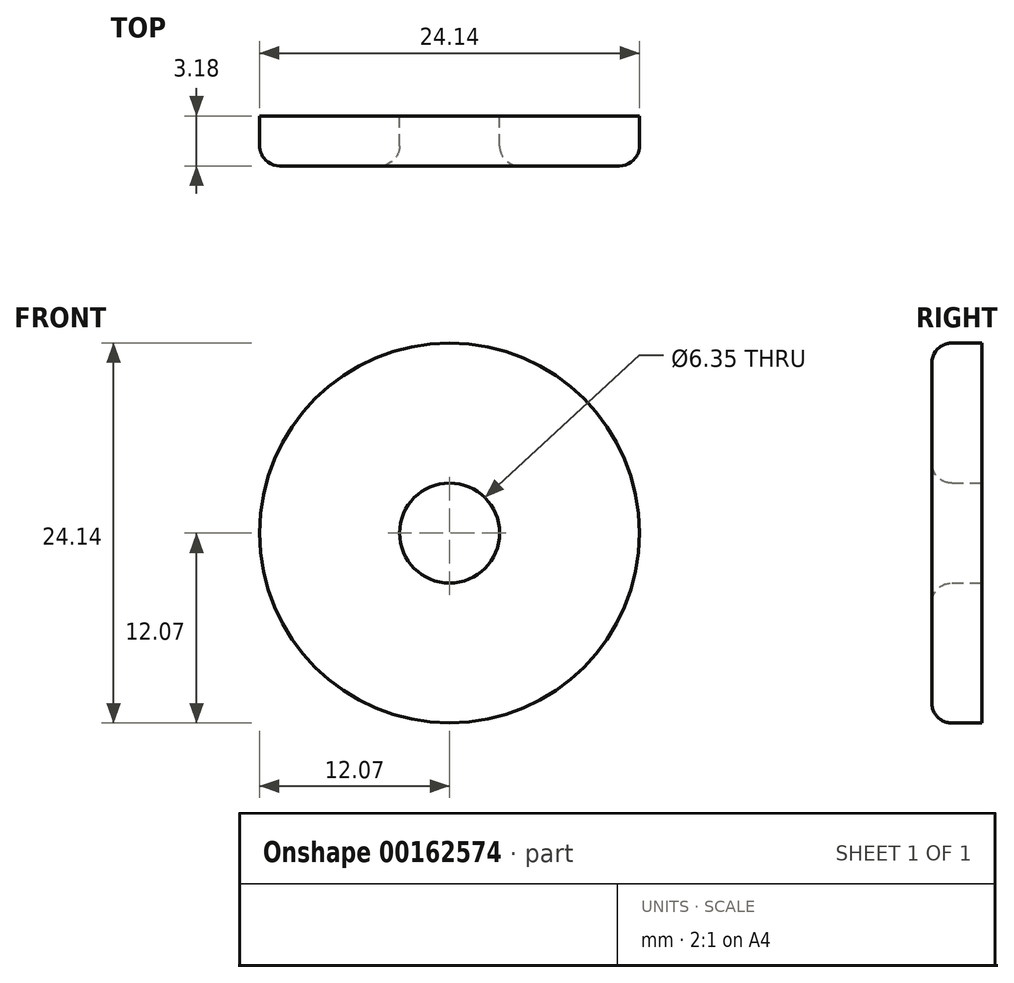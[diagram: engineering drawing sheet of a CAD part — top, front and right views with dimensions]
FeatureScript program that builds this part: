
annotation { "Feature Type Name" : "Feature", "Feature Type Description" : "" }
export const myFeature = defineFeature(function(context is Context, id is Id, definition is map)
    precondition{}
    {
        {
            var Q0;
            Q0=qCreatedBy(makeId("Front.planeOp"),FACE);
            var sketch = newSketch(context, id + "F0", { "sketchPlane" : qUnion([Q0])});
            skCircle(sketch, "E0", {"center": v(0, 0) * mm, "radius": 12.07 * mm});
            skCircle(sketch, "E1", {"center": v(0, 0) * mm, "radius": 3.18 * mm});
            skSolve(sketch);
        }
        {
            var Q0;
            Q0 = qSketchRegion(id + "F0", true);
            extrude(context, id + "F1", {"entities" : qUnion([Q0]), "depth" : 3.17 * mm});
        }
        {
            var Q0;
            Q0=makeQuery(id+"F1.opExtrude","CAP_FACE",FACE,{"disambiguationData":[OSD([sQuery(id+"F0.wireOp",EDGE,"E0"),sQuery(id+"F0.wireOp",EDGE,"E1")])],"isStart":false});
            var Q1;
            Q1=makeQuery(id+"F1.opExtrude","CAP_EDGE",EDGE,{"disambiguationData":[OSD([sQuery(id+"F0.wireOp",EDGE,"E1")])],"isStart":false});
            var Q2;
            Q2=makeQuery(id+"F1.opExtrude","CAP_EDGE",EDGE,{"disambiguationData":[OSD([sQuery(id+"F0.wireOp",EDGE,"E0")])],"isStart":false});
            fillet(context, id + "F2", {"entities" : qUnion([Q0, Q1, Q2]), "radius" : 1.27 * mm, "tangentPropagation" : true, "allowEdgeOverflow" : false});
        }
    });
